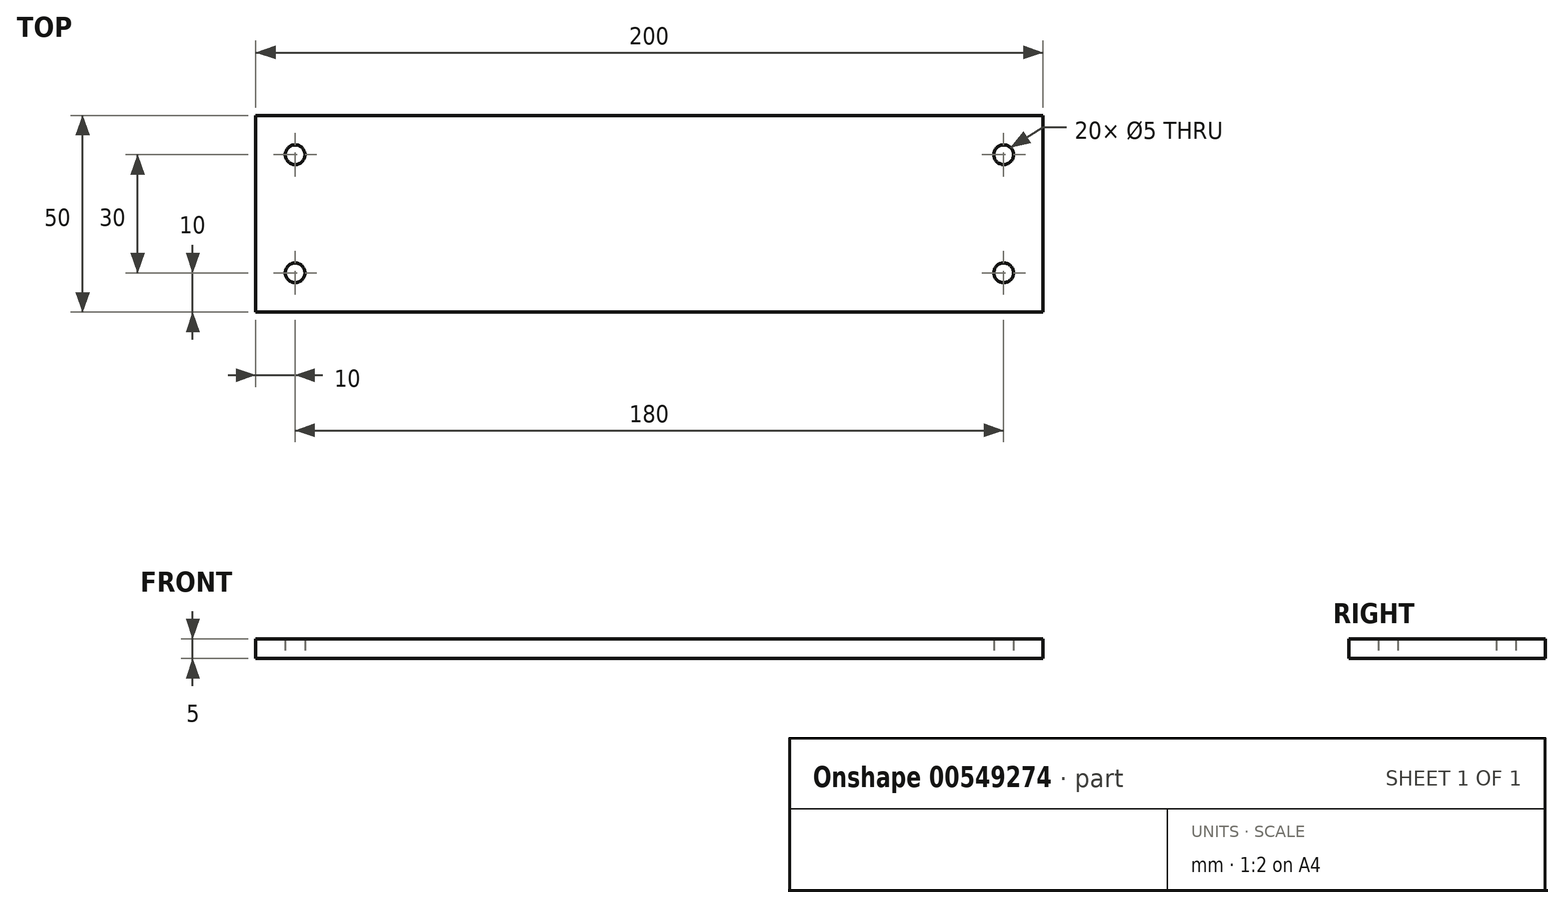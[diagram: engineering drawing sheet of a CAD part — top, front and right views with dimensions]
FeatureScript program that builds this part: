
annotation { "Feature Type Name" : "Feature", "Feature Type Description" : "" }
export const myFeature = defineFeature(function(context is Context, id is Id, definition is map)
    precondition{}
    {
        {
            var Q0;
            Q0=qCreatedBy(makeId("Top.planeOp"),FACE);
            var sketch = newSketch(context, id + "F0", { "sketchPlane" : qUnion([Q0])});
            skLineSegment(sketch, "E0.bottom", {"start": v(-100, 25) * mm, "end": v(100, 25) * mm});
            skLineSegment(sketch, "E0.top", {"start": v(-100, -25) * mm, "end": v(100, -25) * mm});
            skLineSegment(sketch, "E0.left", {"start": v(-100, 25) * mm, "end": v(-100, -25) * mm});
            skLineSegment(sketch, "E0.right", {"start": v(100, 25) * mm, "end": v(100, -25) * mm});
            skPoint(sketch, "E0.middle", {"position": v(0, 0) * mm});
            skCircle(sketch, "E1", {"center": v(-90, 15) * mm, "radius": 2.5 * mm});
            skCircle(sketch, "E2", {"center": v(-90, -15) * mm, "radius": 2.5 * mm});
            skCircle(sketch, "E3", {"center": v(90, 15) * mm, "radius": 2.5 * mm});
            skCircle(sketch, "E4", {"center": v(90, -15) * mm, "radius": 2.5 * mm});
            skSolve(sketch);
        }
        {
            var Q0;
            Q0=makeQuery(id+"F0.imprint","IMPRINT",FACE,{"disambiguationData":[TD([[makeQuery(id+"F0.imprint","IMPRINT",EDGE,{"derivedFrom":sQuery(id+"F0.wireOp",EDGE,"E0.bottom")}),-1.0]])]});
            extrude(context, id + "F1", {"entities" : qUnion([Q0]), "depth" : 5 * mm, "offsetDistance" : 25 * mm});
        }
    });
